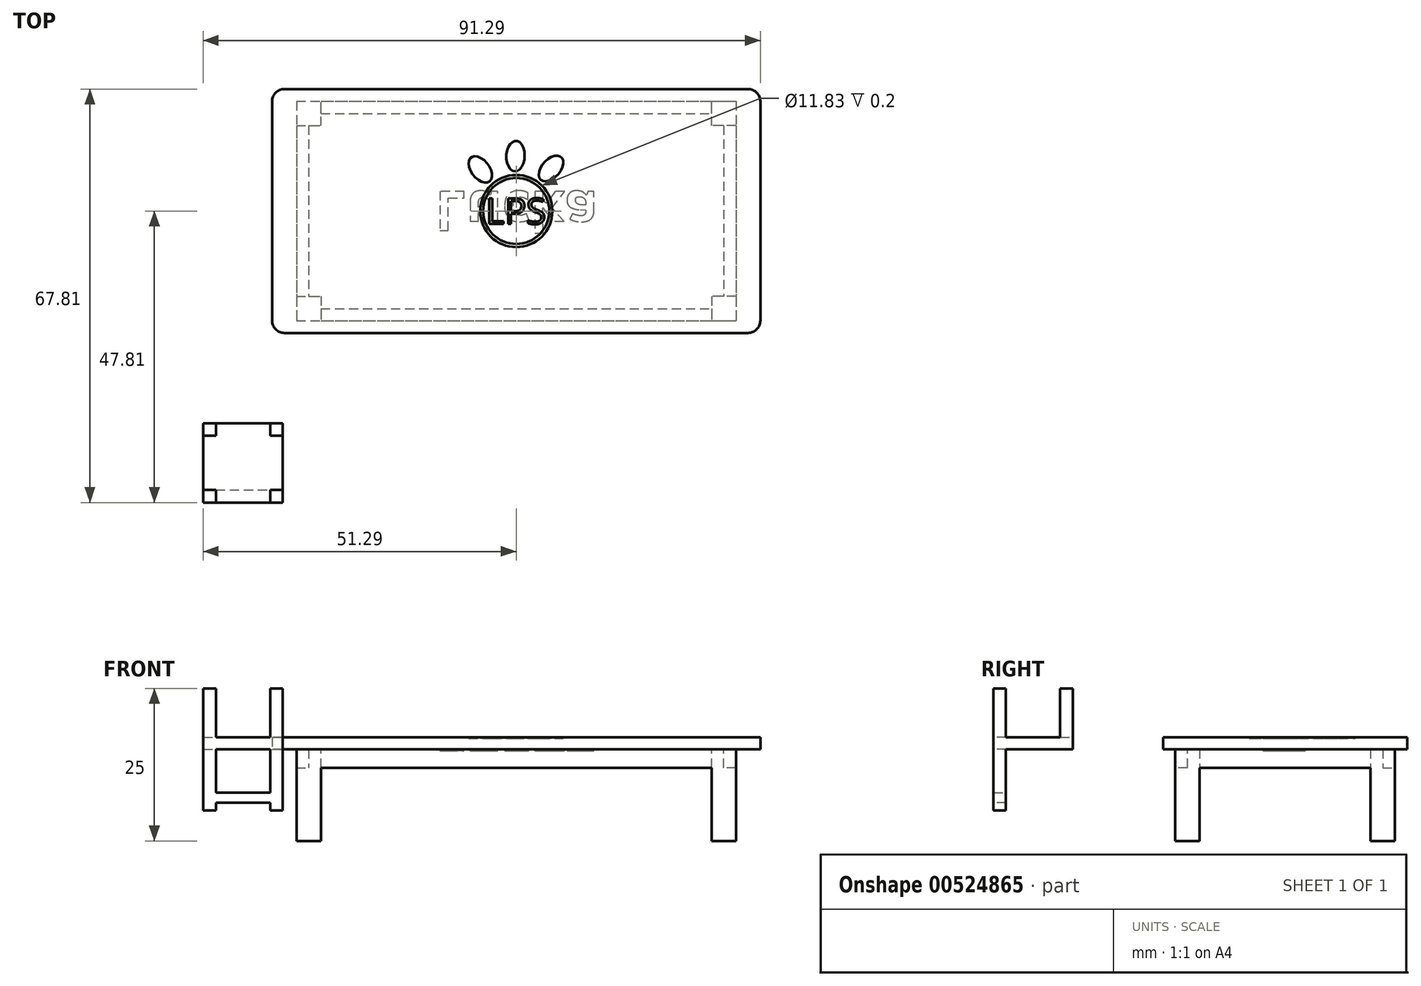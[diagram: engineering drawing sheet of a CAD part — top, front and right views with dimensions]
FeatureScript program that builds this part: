
annotation { "Feature Type Name" : "Feature", "Feature Type Description" : "" }
export const myFeature = defineFeature(function(context is Context, id is Id, definition is map)
    precondition{}
    {
        {
            assignVariable(context, id + "F0", {"name" : "vyska", "anyValue" : 40 * mm});
        }
        {
            var Q0;
            Q0=qCreatedBy(makeId("Top.planeOp"),FACE);
            var sketch = newSketch(context, id + "F1", { "sketchPlane" : qUnion([Q0])});
            skLineSegment(sketch, "E0.bottom", {"start": v(40, 20) * mm, "end": v(-40, 20) * mm});
            skLineSegment(sketch, "E0.top", {"start": v(40, -20) * mm, "end": v(-40, -20) * mm});
            skLineSegment(sketch, "E0.left", {"start": v(40, 20) * mm, "end": v(40, -20) * mm});
            skLineSegment(sketch, "E0.right", {"start": v(-40, 20) * mm, "end": v(-40, -20) * mm});
            skPoint(sketch, "E0.middle", {"position": v(0, 0) * mm});
            skSolve(sketch);
        }
        {
            assignVariable(context, id + "F2", {"name" : "tloustka_desky", "anyValue" : 2 * mm});
        }
        {
            var Q0;
            Q0=makeQuery(id+"F1.imprint","IMPRINT",FACE,{"disambiguationData":[TD([[makeQuery(id+"F1.imprint","IMPRINT",EDGE,{"derivedFrom":sQuery(id+"F1.wireOp",EDGE,"E0.bottom")}),1.0]])]});
            extrude(context, id + "F3", {"entities" : qUnion([Q0]), "depth" : getVariable(context, 'tloustka_desky'), "offsetDistance" : 25 * mm});
        }
        {
            var Q0;
            Q0=makeQuery(id+"F3.opExtrude","CAP_FACE",FACE,{"disambiguationData":[OSD([sQuery(id+"F1.wireOp",EDGE,"E0.bottom"),sQuery(id+"F1.wireOp",EDGE,"E0.top"),sQuery(id+"F1.wireOp",EDGE,"E0.left"),sQuery(id+"F1.wireOp",EDGE,"E0.right")])],"isStart":true});
            var sketch = newSketch(context, id + "F4", { "sketchPlane" : qUnion([Q0])});
            skLineSegment(sketch, "E1", {"start": v(-73.34, -36.67) * mm, "end": v(97.16, 48.58) * mm, "construction": true});
            skLineSegment(sketch, "E2", {"start": v(-70.65, 0) * mm, "end": v(92.9, 0) * mm, "construction": true});
            skLineSegment(sketch, "E3", {"start": v(0, 54.19) * mm, "end": v(0, -56.35) * mm, "construction": true});
            skLineSegment(sketch, "E4.bottom", {"start": v(-36, -18) * mm, "end": v(36, -18) * mm});
            skLineSegment(sketch, "E4.top", {"start": v(-36, 18) * mm, "end": v(36, 18) * mm});
            skLineSegment(sketch, "E4.left", {"start": v(-36, -18) * mm, "end": v(-36, 18) * mm});
            skLineSegment(sketch, "E4.right", {"start": v(36, -18) * mm, "end": v(36, 18) * mm});
            skPoint(sketch, "E4.middle", {"position": v(0, 0) * mm});
            skLineSegment(sketch, "E5", {"start": v(-36, -14) * mm, "end": v(-32, -14) * mm});
            skLineSegment(sketch, "E6", {"start": v(-32, -14) * mm, "end": v(-32, -18) * mm});
            skLineSegment(sketch, "E7.MirrorCS", {"start": v(36, -14) * mm, "end": v(32, -14) * mm});
            skLineSegment(sketch, "E8.MirrorCS", {"start": v(32, -14) * mm, "end": v(32, -18) * mm});
            skLineSegment(sketch, "E9.MirrorCS", {"start": v(-36, 14) * mm, "end": v(-32, 14) * mm});
            skLineSegment(sketch, "E10.MirrorCS", {"start": v(-32, 14) * mm, "end": v(-32, 18) * mm});
            skLineSegment(sketch, "E11.MirrorCS", {"start": v(32, 14) * mm, "end": v(32, 18) * mm});
            skLineSegment(sketch, "E12.MirrorCS", {"start": v(36, 14) * mm, "end": v(32, 14) * mm});
            skLineSegment(sketch, "E13.bottom", {"start": v(-34, -16) * mm, "end": v(34, -16) * mm});
            skLineSegment(sketch, "E13.top", {"start": v(-34, 16) * mm, "end": v(34, 16) * mm});
            skLineSegment(sketch, "E13.left", {"start": v(-34, -16) * mm, "end": v(-34, 16) * mm});
            skLineSegment(sketch, "E13.right", {"start": v(34, -16) * mm, "end": v(34, 16) * mm});
            skSolve(sketch);
        }
        {
            assignVariable(context, id + "F5", {"name" : "vyska", "anyValue" : 17 * mm});
        }
        {
            var Q0;
            {var subQ0=sQuery(id+"F4.wireOp",EDGE,"1s5hToEE-7Yhg-MsuK-7zEi-yVWtRCPxNcyl.left");var subQ1=sQuery(id+"F4.wireOp",EDGE,"1s5hToEE-7Yhg-MsuK-7zEi-yVWtRCPxNcyl.top");var subQ2=makeQuery(id+"F4.imprint","INTERSECT",VERTEX,{"derivedFrom":[subQ1,subQ0]});Q0=makeQuery(id+"F4.imprint","IMPRINT",FACE,{"disambiguationData":[TD([[makeQuery(id+"F4.imprint","IMPRINT",EDGE,{"disambiguationData":[TD([[subQ2,-1.0]])],"derivedFrom":subQ1}),-1.0]])]});}
            var Q1;
            {var subQ7=sQuery(id+"F4.wireOp",EDGE,"E4.left");var subQ8=sQuery(id+"F4.wireOp",EDGE,"E4.top");var subQ9=makeQuery(id+"F4.imprint","INTERSECT",VERTEX,{"derivedFrom":[subQ8,subQ7]});Q1=makeQuery(id+"F4.imprint","IMPRINT",FACE,{"disambiguationData":[TD([[makeQuery(id+"F4.imprint","IMPRINT",EDGE,{"disambiguationData":[TD([[subQ9,-1.0]])],"derivedFrom":subQ8}),-1.0]])]});}
            var Q2;
            {var subQ0=sQuery(id+"F4.wireOp",EDGE,"1s5hToEE-7Yhg-MsuK-7zEi-yVWtRCPxNcyl.right");var subQ1=sQuery(id+"F4.wireOp",EDGE,"1s5hToEE-7Yhg-MsuK-7zEi-yVWtRCPxNcyl.top");var subQ2=makeQuery(id+"F4.imprint","INTERSECT",VERTEX,{"derivedFrom":[subQ1,subQ0]});Q2=makeQuery(id+"F4.imprint","IMPRINT",FACE,{"disambiguationData":[TD([[makeQuery(id+"F4.imprint","IMPRINT",EDGE,{"disambiguationData":[TD([[subQ2,1.0]])],"derivedFrom":subQ1}),-1.0]])]});}
            var Q3;
            {var subQ7=sQuery(id+"F4.wireOp",EDGE,"E4.left");var subQ8=sQuery(id+"F4.wireOp",EDGE,"E4.bottom");var subQ9=makeQuery(id+"F4.imprint","INTERSECT",VERTEX,{"derivedFrom":[subQ8,subQ7]});Q3=makeQuery(id+"F4.imprint","IMPRINT",FACE,{"disambiguationData":[TD([[makeQuery(id+"F4.imprint","IMPRINT",EDGE,{"disambiguationData":[TD([[subQ9,-1.0]])],"derivedFrom":subQ8}),1.0]])]});}
            var Q4;
            {var subQ7=sQuery(id+"F4.wireOp",EDGE,"E4.right");var subQ8=sQuery(id+"F4.wireOp",EDGE,"E4.bottom");var subQ9=makeQuery(id+"F4.imprint","INTERSECT",VERTEX,{"derivedFrom":[subQ8,subQ7]});Q4=makeQuery(id+"F4.imprint","IMPRINT",FACE,{"disambiguationData":[TD([[makeQuery(id+"F4.imprint","IMPRINT",EDGE,{"disambiguationData":[TD([[subQ9,1.0]])],"derivedFrom":subQ8}),1.0]])]});}
            var Q5;
            {var subQ0=sQuery(id+"F4.wireOp",EDGE,"E10.MirrorCS");var subQ1=sQuery(id+"F4.wireOp",EDGE,"E9.MirrorCS");var subQ2=makeQuery(id+"F4.imprint","INTERSECT",VERTEX,{"derivedFrom":[subQ1,subQ0]});Q5=makeQuery(id+"F4.imprint","IMPRINT",FACE,{"disambiguationData":[TD([[makeQuery(id+"F4.imprint","IMPRINT",EDGE,{"disambiguationData":[TD([[subQ2,1.0]])],"derivedFrom":subQ1}),1.0]])]});}
            var Q6;
            {var subQ0=sQuery(id+"F4.wireOp",EDGE,"E6");var subQ1=sQuery(id+"F4.wireOp",EDGE,"E5");var subQ2=makeQuery(id+"F4.imprint","INTERSECT",VERTEX,{"derivedFrom":[subQ1,subQ0]});Q6=makeQuery(id+"F4.imprint","IMPRINT",FACE,{"disambiguationData":[TD([[makeQuery(id+"F4.imprint","IMPRINT",EDGE,{"disambiguationData":[TD([[subQ2,1.0]])],"derivedFrom":subQ1}),-1.0]])]});}
            var Q7;
            {var subQ0=sQuery(id+"F4.wireOp",EDGE,"E8.MirrorCS");var subQ1=sQuery(id+"F4.wireOp",EDGE,"E7.MirrorCS");var subQ2=makeQuery(id+"F4.imprint","INTERSECT",VERTEX,{"derivedFrom":[subQ1,subQ0]});Q7=makeQuery(id+"F4.imprint","IMPRINT",FACE,{"disambiguationData":[TD([[makeQuery(id+"F4.imprint","IMPRINT",EDGE,{"disambiguationData":[TD([[subQ2,1.0]])],"derivedFrom":subQ1}),1.0]])]});}
            var Q8;
            {var subQ0=sQuery(id+"F4.wireOp",EDGE,"E12.MirrorCS");var subQ1=sQuery(id+"F4.wireOp",EDGE,"E11.MirrorCS");var subQ2=makeQuery(id+"F4.imprint","INTERSECT",VERTEX,{"derivedFrom":[subQ1,subQ0]});Q8=makeQuery(id+"F4.imprint","IMPRINT",FACE,{"disambiguationData":[TD([[makeQuery(id+"F4.imprint","IMPRINT",EDGE,{"disambiguationData":[TD([[subQ2,-1.0]])],"derivedFrom":subQ1}),-1.0]])]});}
            var Q9;
            {var subQ1=sQuery(id+"F4.wireOp",EDGE,"E4.right");var subQ5=sQuery(id+"F4.wireOp",EDGE,"E4.top");var subQ6=makeQuery(id+"F4.imprint","INTERSECT",VERTEX,{"derivedFrom":[subQ5,subQ1]});Q9=makeQuery(id+"F4.imprint","IMPRINT",FACE,{"disambiguationData":[TD([[makeQuery(id+"F4.imprint","IMPRINT",EDGE,{"disambiguationData":[TD([[subQ6,1.0]])],"derivedFrom":subQ5}),-1.0]])]});}
            extrude(context, id + "F6", {"entities" : qUnion([Q0, Q1, Q2, Q3, Q4, Q5, Q6, Q7, Q8, Q9]), "operationType" : NewBodyOperationType.ADD, "depth" : getVariable(context, 'vyska') - getVariable(context, 'tloustka_desky'), "offsetDistance" : 25 * mm});
        }
        {
            var Q0;
            {var subQ0=sQuery(id+"F4.wireOp",EDGE,"E5");var subQ1=sQuery(id+"F4.wireOp",EDGE,"E4.left");var subQ2=makeQuery(id+"F4.imprint","INTERSECT",VERTEX,{"derivedFrom":[subQ1,subQ0]});Q0=makeQuery(id+"F4.imprint","IMPRINT",FACE,{"disambiguationData":[TD([[makeQuery(id+"F4.imprint","IMPRINT",EDGE,{"disambiguationData":[TD([[subQ2,-1.0]])],"derivedFrom":subQ1}),-1.0]])]});}
            var Q1;
            {var subQ0=sQuery(id+"F4.wireOp",EDGE,"E10.MirrorCS");var subQ1=sQuery(id+"F4.wireOp",EDGE,"E4.top");var subQ2=makeQuery(id+"F4.imprint","INTERSECT",VERTEX,{"derivedFrom":[subQ1,subQ0]});Q1=makeQuery(id+"F4.imprint","IMPRINT",FACE,{"disambiguationData":[TD([[makeQuery(id+"F4.imprint","IMPRINT",EDGE,{"disambiguationData":[TD([[subQ2,-1.0]])],"derivedFrom":subQ1}),-1.0]])]});}
            var Q2;
            {var subQ0=sQuery(id+"F4.wireOp",EDGE,"E7.MirrorCS");var subQ1=sQuery(id+"F4.wireOp",EDGE,"E4.right");var subQ2=makeQuery(id+"F4.imprint","INTERSECT",VERTEX,{"derivedFrom":[subQ1,subQ0]});Q2=makeQuery(id+"F4.imprint","IMPRINT",FACE,{"disambiguationData":[TD([[makeQuery(id+"F4.imprint","IMPRINT",EDGE,{"disambiguationData":[TD([[subQ2,-1.0]])],"derivedFrom":subQ1}),1.0]])]});}
            var Q3;
            {var subQ0=sQuery(id+"F4.wireOp",EDGE,"E6");var subQ1=sQuery(id+"F4.wireOp",EDGE,"E4.bottom");var subQ2=makeQuery(id+"F4.imprint","INTERSECT",VERTEX,{"derivedFrom":[subQ1,subQ0]});Q3=makeQuery(id+"F4.imprint","IMPRINT",FACE,{"disambiguationData":[TD([[makeQuery(id+"F4.imprint","IMPRINT",EDGE,{"disambiguationData":[TD([[subQ2,-1.0]])],"derivedFrom":subQ1}),1.0]])]});}
            var Q4;
            {var subQ1=sQuery(id+"F4.wireOp",EDGE,"E4.right");var subQ5=sQuery(id+"F4.wireOp",EDGE,"E4.top");var subQ6=makeQuery(id+"F4.imprint","INTERSECT",VERTEX,{"derivedFrom":[subQ5,subQ1]});Q4=makeQuery(id+"F4.imprint","IMPRINT",FACE,{"disambiguationData":[TD([[makeQuery(id+"F4.imprint","IMPRINT",EDGE,{"disambiguationData":[TD([[subQ6,1.0]])],"derivedFrom":subQ5}),-1.0]])]});}
            var Q5;
            {var subQ1=sQuery(id+"F4.wireOp",EDGE,"E4.left");var subQ9=sQuery(id+"F4.wireOp",EDGE,"E4.top");var subQ11=makeQuery(id+"F4.imprint","INTERSECT",VERTEX,{"derivedFrom":[subQ9,subQ1]});Q5=makeQuery(id+"F4.imprint","IMPRINT",FACE,{"disambiguationData":[TD([[makeQuery(id+"F4.imprint","IMPRINT",EDGE,{"disambiguationData":[TD([[subQ11,-1.0]])],"derivedFrom":subQ9}),-1.0]])]});}
            var Q6;
            {var subQ1=sQuery(id+"F4.wireOp",EDGE,"E4.left");var subQ7=sQuery(id+"F4.wireOp",EDGE,"E4.bottom");var subQ8=makeQuery(id+"F4.imprint","INTERSECT",VERTEX,{"derivedFrom":[subQ7,subQ1]});Q6=makeQuery(id+"F4.imprint","IMPRINT",FACE,{"disambiguationData":[TD([[makeQuery(id+"F4.imprint","IMPRINT",EDGE,{"disambiguationData":[TD([[subQ8,-1.0]])],"derivedFrom":subQ7}),1.0]])]});}
            var Q7;
            {var subQ1=sQuery(id+"F4.wireOp",EDGE,"E4.right");var subQ6=sQuery(id+"F4.wireOp",EDGE,"E4.bottom");var subQ11=makeQuery(id+"F4.imprint","INTERSECT",VERTEX,{"derivedFrom":[subQ6,subQ1]});Q7=makeQuery(id+"F4.imprint","IMPRINT",FACE,{"disambiguationData":[TD([[makeQuery(id+"F4.imprint","IMPRINT",EDGE,{"disambiguationData":[TD([[subQ11,1.0]])],"derivedFrom":subQ6}),1.0]])]});}
            extrude(context, id + "F7", {"entities" : qUnion([Q0, Q1, Q2, Q3, Q4, Q5, Q6, Q7]), "operationType" : NewBodyOperationType.ADD, "depth" : getVariable(context, 'tloustka_desky') * 1.5, "offsetDistance" : 25 * mm});
        }
        {
            var Q0;
            Q0=makeQuery(id+"F3.opExtrude","SWEPT_EDGE",EDGE,{"disambiguationData":[OSD([sQuery(id+"F1.wireOp",EDGE,"E0.top"),sQuery(id+"F1.wireOp",EDGE,"E0.right")])]});
            var Q1;
            Q1=makeQuery(id+"F3.opExtrude","SWEPT_EDGE",EDGE,{"disambiguationData":[OSD([sQuery(id+"F1.wireOp",EDGE,"E0.top"),sQuery(id+"F1.wireOp",EDGE,"E0.left")])]});
            var Q2;
            Q2=makeQuery(id+"F3.opExtrude","SWEPT_EDGE",EDGE,{"disambiguationData":[OSD([sQuery(id+"F1.wireOp",EDGE,"E0.bottom"),sQuery(id+"F1.wireOp",EDGE,"E0.left")])]});
            var Q3;
            Q3=makeQuery(id+"F3.opExtrude","SWEPT_EDGE",EDGE,{"disambiguationData":[OSD([sQuery(id+"F1.wireOp",EDGE,"E0.bottom"),sQuery(id+"F1.wireOp",EDGE,"E0.right")])]});
            fillet(context, id + "F8", {"entities" : qUnion([Q0, Q1, Q2, Q3]), "radius" : getVariable(context, 'tloustka_desky'), "tangentPropagation" : true, "allowEdgeOverflow" : false});
        }
        {
            var Q0;
            Q0=makeQuery(id+"F7.boolean.opBoolean","SPLIT",FACE,{"disambiguationData":[TD([makeQuery(id+"F6.opExtrude","SWEPT_FACE",FACE,{"disambiguationData":[OSD([sQuery(id+"F4.wireOp",EDGE,"E5")])]})])],"derivedFrom":makeQuery(id+"F3.opExtrude","CAP_FACE",FACE,{"disambiguationData":[OSD([sQuery(id+"F1.wireOp",EDGE,"E0.bottom"),sQuery(id+"F1.wireOp",EDGE,"E0.top"),sQuery(id+"F1.wireOp",EDGE,"E0.left"),sQuery(id+"F1.wireOp",EDGE,"E0.right")])],"isStart":true})});
            var sketch = newSketch(context, id + "F9", { "sketchPlane" : qUnion([Q0])});
            skText(sketch, "E14", { "text": "Lucka", "fontName": "OpenSans-Bold.ttf"});
            skLineSegment(sketch, "E15", {"start": v(-13.33, -3.25) * mm, "end": v(13.33, 3.25) * mm, "construction": true});
            skLineSegment(sketch, "E16", {"start": v(-13.33, 3.25) * mm, "end": v(13.33, -3.25) * mm, "construction": true});
            skPoint(sketch, "E17", {"position": v(0, 0) * mm});
            const initialGuessF9  = {"E14": [-0.01333, -0.00325, 1, 0, 0.0065]};
            skSetInitialGuess(sketch, initialGuessF9);
            skSolve(sketch);
        }
        {
            assignVariable(context, id + "F10", {"name" : "pismo", "anyValue" : 0.2 * mm});
        }
        {
            var Q0;
            Q0=makeQuery(id+"F9.imprint","IMPRINT",FACE,{"disambiguationData":[TD([[makeQuery(id+"F9.imprint","IMPRINT",EDGE,{"derivedFrom":sQuery(id+"F9.wireOp",EDGE,"E14.sketch_text.stroke-0")}),-1.0]])]});
            var Q1;
            Q1=makeQuery(id+"F9.imprint","IMPRINT",FACE,{"disambiguationData":[TD([[makeQuery(id+"F9.imprint","IMPRINT",EDGE,{"derivedFrom":sQuery(id+"F9.wireOp",EDGE,"E14.sketch_text.stroke-14")}),-1.0]])]});
            var Q2;
            Q2=makeQuery(id+"F9.imprint","IMPRINT",FACE,{"disambiguationData":[TD([[makeQuery(id+"F9.imprint","IMPRINT",EDGE,{"derivedFrom":sQuery(id+"F9.wireOp",EDGE,"E14.sketch_text.stroke-38")}),-1.0]])]});
            var Q3;
            Q3=makeQuery(id+"F9.imprint","IMPRINT",FACE,{"disambiguationData":[TD([[makeQuery(id+"F9.imprint","IMPRINT",EDGE,{"derivedFrom":sQuery(id+"F9.wireOp",EDGE,"E14.sketch_text.stroke-62")}),-1.0]])]});
            var Q4;
            Q4=makeQuery(id+"F9.imprint","IMPRINT",FACE,{"disambiguationData":[TD([[makeQuery(id+"F9.imprint","IMPRINT",EDGE,{"derivedFrom":sQuery(id+"F9.wireOp",EDGE,"E14.sketch_text.stroke-78")}),-1.0]])]});
            var Q5;
            Q5=makeQuery(id+"F9.imprint","IMPRINT",FACE,{"disambiguationData":[TD([[makeQuery(id+"F9.imprint","IMPRINT",EDGE,{"derivedFrom":sQuery(id+"F9.wireOp",EDGE,"E14.sketch_text.stroke-88")}),-1.0]])]});
            var Q6;
            Q6=makeQuery(id+"F9.imprint","IMPRINT",FACE,{"disambiguationData":[TD([[makeQuery(id+"F9.imprint","IMPRINT",EDGE,{"derivedFrom":sQuery(id+"F9.wireOp",EDGE,"E14.sketch_text.stroke-95")}),-1.0]])]});
            var Q7;
            Q7=makeQuery(id+"F9.imprint","IMPRINT",FACE,{"disambiguationData":[TD([[makeQuery(id+"F9.imprint","IMPRINT",EDGE,{"derivedFrom":sQuery(id+"F9.wireOp",EDGE,"E14.sketch_text.stroke-105")}),-1.0]])]});
            var Q8;
            Q8=makeQuery(id+"F9.imprint","IMPRINT",FACE,{"disambiguationData":[TD([[makeQuery(id+"F9.imprint","IMPRINT",EDGE,{"derivedFrom":sQuery(id+"F9.wireOp",EDGE,"E14.sketch_text.stroke-128")}),-1.0]])]});
            var Q9;
            Q9=makeQuery(id+"F9.imprint","IMPRINT",FACE,{"disambiguationData":[TD([[makeQuery(id+"F9.imprint","IMPRINT",EDGE,{"derivedFrom":sQuery(id+"F9.wireOp",EDGE,"E14.sketch_text.stroke-23")}),-1.0]])]});
            extrude(context, id + "F11", {"entities" : qUnion([Q0, Q1, Q2, Q3, Q4, Q5, Q6, Q7, Q8, Q9]), "operationType" : NewBodyOperationType.ADD, "depth" : getVariable(context, 'pismo'), "offsetDistance" : 25 * mm});
        }
        {
            var Q0;
            Q0=makeQuery(id+"F3.opExtrude","CAP_FACE",FACE,{"disambiguationData":[OSD([sQuery(id+"F1.wireOp",EDGE,"E0.bottom"),sQuery(id+"F1.wireOp",EDGE,"E0.top"),sQuery(id+"F1.wireOp",EDGE,"E0.left"),sQuery(id+"F1.wireOp",EDGE,"E0.right")])],"isStart":false});
            var sketch = newSketch(context, id + "F12", { "sketchPlane" : qUnion([Q0])});
            skText(sketch, "E18", { "text": "LPS", "fontName": "OpenSans-Regular.ttf"});
            skLineSegment(sketch, "E19", {"start": v(-4.98, -2.13) * mm, "end": v(4.98, 2.12) * mm, "construction": true});
            skLineSegment(sketch, "E20", {"start": v(-4.98, 2.13) * mm, "end": v(4.98, -2.13) * mm, "construction": true});
            skPoint(sketch, "E21", {"position": v(0, 0) * mm});
            skCircle(sketch, "E22", {"center": v(0, 0) * mm, "radius": 5.41 * mm});
            skCircle(sketch, "E23", {"center": v(0, 0) * mm, "radius": 5.91 * mm});
            skLineSegment(sketch, "E24", {"start": v(0, 0) * mm, "end": v(-7.22, 8.38) * mm, "construction": true});
            skEllipse(sketch, "E25", {"center": v(-5.88, 6.82) * mm, "majorRadius": 2.5 * mm, "minorRadius": 1.5 * mm, "majorAxis": v(0.61, -0.8)});
            skEllipse(sketch, "E26.1.0", {"center": v(-0.12, 9) * mm, "majorRadius": 2.5 * mm, "minorRadius": 1.5 * mm, "majorAxis": v(-0.04, -1)});
            skEllipse(sketch, "E26.2.0", {"center": v(5.7, 6.97) * mm, "majorRadius": 2.5 * mm, "minorRadius": 1.5 * mm, "majorAxis": v(-0.67, -0.74)});
            skLineSegment(sketch, "E26.anchor1", {"start": v(0, 0) * mm, "end": v(-5.88, 6.82) * mm, "construction": true});
            skLineSegment(sketch, "E26.anchor2", {"start": v(0, 0) * mm, "end": v(5.7, 6.97) * mm, "construction": true});
            const initialGuessF12  = {"E18": [-0.00498, -0.00213, 1, 0, 0.00425]};
            skSetInitialGuess(sketch, initialGuessF12);
            skSolve(sketch);
        }
        {
            var Q0;
            Q0=makeQuery(id+"F12.imprint","IMPRINT",FACE,{"disambiguationData":[TD([[makeQuery(id+"F12.imprint","IMPRINT",EDGE,{"derivedFrom":sQuery(id+"F12.wireOp",EDGE,"E18.sketch_text.stroke-0")}),-1.0]])]});
            var Q1;
            Q1=makeQuery(id+"F12.imprint","IMPRINT",FACE,{"disambiguationData":[TD([[makeQuery(id+"F12.imprint","IMPRINT",EDGE,{"derivedFrom":sQuery(id+"F12.wireOp",EDGE,"E18.sketch_text.stroke-6")}),-1.0]])]});
            var Q2;
            Q2=makeQuery(id+"F12.imprint","IMPRINT",FACE,{"disambiguationData":[TD([[makeQuery(id+"F12.imprint","IMPRINT",EDGE,{"derivedFrom":sQuery(id+"F12.wireOp",EDGE,"E18.sketch_text.stroke-21")}),-1.0]])]});
            var Q3;
            Q3=makeQuery(id+"F12.imprint","IMPRINT",FACE,{"disambiguationData":[TD([[makeQuery(id+"F12.imprint","IMPRINT",EDGE,{"derivedFrom":sQuery(id+"F12.wireOp",EDGE,"E22")}),-1.0]])]});
            var Q4;
            Q4=makeQuery(id+"F12.imprint","IMPRINT",FACE,{"disambiguationData":[TD([[makeQuery(id+"F12.imprint","IMPRINT",EDGE,{"derivedFrom":sQuery(id+"F12.wireOp",EDGE,"E25")}),1.0]])]});
            var Q5;
            Q5=makeQuery(id+"F12.imprint","IMPRINT",FACE,{"disambiguationData":[TD([[makeQuery(id+"F12.imprint","IMPRINT",EDGE,{"derivedFrom":sQuery(id+"F12.wireOp",EDGE,"E26.1.0")}),1.0]])]});
            var Q6;
            Q6=makeQuery(id+"F12.imprint","IMPRINT",FACE,{"disambiguationData":[TD([[makeQuery(id+"F12.imprint","IMPRINT",EDGE,{"derivedFrom":sQuery(id+"F12.wireOp",EDGE,"E26.2.0")}),1.0]])]});
            extrude(context, id + "F13", {"entities" : qUnion([Q0, Q1, Q2, Q3, Q4, Q5, Q6]), "operationType" : NewBodyOperationType.REMOVE, "oppositeDirection" : true, "depth" : getVariable(context, 'pismo'), "offsetDistance" : 25 * mm});
        }
        {
            var Q0;
            Q0=qCreatedBy(makeId("Top.planeOp"),FACE);
            var sketch = newSketch(context, id + "F14", { "sketchPlane" : qUnion([Q0])});
            skLineSegment(sketch, "E27.bottom", {"start": v(-51.29, -34.79) * mm, "end": v(-38.27, -34.79) * mm});
            skLineSegment(sketch, "E27.top", {"start": v(-51.29, -47.8) * mm, "end": v(-38.27, -47.8) * mm});
            skLineSegment(sketch, "E27.left", {"start": v(-51.29, -34.79) * mm, "end": v(-51.29, -47.8) * mm});
            skLineSegment(sketch, "E27.right", {"start": v(-38.27, -34.79) * mm, "end": v(-38.27, -47.8) * mm});
            skLineSegment(sketch, "E28", {"start": v(-51.29, -45.74) * mm, "end": v(-49.22, -45.74) * mm});
            skLineSegment(sketch, "E29", {"start": v(-49.22, -45.74) * mm, "end": v(-49.22, -47.8) * mm});
            skLineSegment(sketch, "E30", {"start": v(-54.35, -31.72) * mm, "end": v(-35.54, -50.53) * mm, "construction": true});
            skLineSegment(sketch, "E31", {"start": v(-54.73, -51.25) * mm, "end": v(-35.92, -32.44) * mm, "construction": true});
            skPoint(sketch, "E32", {"position": v(-44.78, -41.3) * mm});
            skLineSegment(sketch, "E33", {"start": v(-44.78, -30.52) * mm, "end": v(-44.78, -57.12) * mm, "construction": true});
            skLineSegment(sketch, "E34", {"start": v(-55.43, -41.3) * mm, "end": v(-28.83, -41.3) * mm, "construction": true});
            skLineSegment(sketch, "E35.MirrorCS", {"start": v(-40.34, -45.74) * mm, "end": v(-40.34, -47.8) * mm});
            skLineSegment(sketch, "E36.MirrorCS", {"start": v(-38.27, -45.74) * mm, "end": v(-40.34, -45.74) * mm});
            skLineSegment(sketch, "E37.MirrorCS", {"start": v(-51.29, -36.85) * mm, "end": v(-49.22, -36.85) * mm});
            skLineSegment(sketch, "E38.MirrorCS", {"start": v(-49.22, -36.85) * mm, "end": v(-49.22, -34.79) * mm});
            skLineSegment(sketch, "E39.MirrorCS", {"start": v(-40.34, -36.85) * mm, "end": v(-40.34, -34.79) * mm});
            skLineSegment(sketch, "E40.MirrorCS", {"start": v(-38.27, -36.85) * mm, "end": v(-40.34, -36.85) * mm});
            skSolve(sketch);
        }
        {
            var Q0;
            {var subQ4=sQuery(id+"F14.wireOp",EDGE,"E28");Q0=makeQuery(id+"F14.imprint","IMPRINT",FACE,{"disambiguationData":[TD([[makeQuery(id+"F14.imprint","IMPRINT",EDGE,{"derivedFrom":subQ4}),-1.0]])]});}
            var Q1;
            {var subQ3=sQuery(id+"F14.wireOp",EDGE,"E35.MirrorCS");Q1=makeQuery(id+"F14.imprint","IMPRINT",FACE,{"disambiguationData":[TD([[makeQuery(id+"F14.imprint","IMPRINT",EDGE,{"derivedFrom":subQ3}),1.0]])]});}
            extrude(context, id + "F15", {"entities" : qUnion([Q0, Q1]), "depth" : 10 * mm, "offsetDistance" : 25 * mm, "hasSecondDirection" : true, "secondDirectionOppositeDirection" : true, "secondDirectionDepth" : 10 * mm});
        }
        {
            var Q0;
            {var subQ4=sQuery(id+"F14.wireOp",EDGE,"E37.MirrorCS");Q0=makeQuery(id+"F14.imprint","IMPRINT",FACE,{"disambiguationData":[TD([[makeQuery(id+"F14.imprint","IMPRINT",EDGE,{"derivedFrom":subQ4}),1.0]])]});}
            var Q1;
            {var subQ3=sQuery(id+"F14.wireOp",EDGE,"E39.MirrorCS");Q1=makeQuery(id+"F14.imprint","IMPRINT",FACE,{"disambiguationData":[TD([[makeQuery(id+"F14.imprint","IMPRINT",EDGE,{"derivedFrom":subQ3}),-1.0]])]});}
            extrude(context, id + "F16", {"entities" : qUnion([Q0, Q1]), "depth" : 10 * mm, "offsetDistance" : 25 * mm});
        }
        {
            var Q0;
            {var subQ4=sQuery(id+"F14.wireOp",EDGE,"E28");Q0=makeQuery(id+"F14.imprint","IMPRINT",FACE,{"disambiguationData":[TD([[makeQuery(id+"F14.imprint","IMPRINT",EDGE,{"derivedFrom":subQ4}),1.0]])]});}
            var Q1;
            {var subQ4=sQuery(id+"F14.wireOp",EDGE,"E37.MirrorCS");Q1=makeQuery(id+"F14.imprint","IMPRINT",FACE,{"disambiguationData":[TD([[makeQuery(id+"F14.imprint","IMPRINT",EDGE,{"derivedFrom":subQ4}),1.0]])]});}
            var Q2;
            {var subQ3=sQuery(id+"F14.wireOp",EDGE,"E39.MirrorCS");Q2=makeQuery(id+"F14.imprint","IMPRINT",FACE,{"disambiguationData":[TD([[makeQuery(id+"F14.imprint","IMPRINT",EDGE,{"derivedFrom":subQ3}),-1.0]])]});}
            extrude(context, id + "F17", {"entities" : qUnion([Q0, Q1, Q2]), "operationType" : NewBodyOperationType.ADD, "depth" : 2 * mm, "offsetDistance" : 25 * mm});
        }
        {
            var Q0;
            {var subQ0=sQuery(id+"F14.wireOp",EDGE,"E36.MirrorCS");var subQ2=sQuery(id+"F14.wireOp",EDGE,"E27.top");var subQ4=sQuery(id+"F14.wireOp",EDGE,"E35.MirrorCS");var subQ5=sQuery(id+"F14.wireOp",EDGE,"E27.right");Q0=makeQuery(id+"F17.boolean.opBoolean","SPLIT",FACE,{"disambiguationData":[TD([makeQuery(id+"F15.opExtrude","CAP_FACE",FACE,{"disambiguationData":[OSD([subQ2,subQ5,subQ4,subQ0])],"isStart":true})])],"derivedFrom":makeQuery(id+"F15.opExtrude","SWEPT_FACE",FACE,{"disambiguationData":[OSD([subQ4])]})});}
            var sketch = newSketch(context, id + "F18", { "sketchPlane" : qUnion([Q0])});
            skLineSegment(sketch, "E41", {"start": v(47.8, -8.71) * mm, "end": v(45.74, -8.71) * mm});
            skLineSegment(sketch, "E42", {"start": v(47.8, -7.08) * mm, "end": v(45.74, -7.08) * mm});
            skSolve(sketch);
        }
        {
            var Q0;
            {var subQ0=sQuery(id+"F18.wireOp",EDGE,"E41");Q0=makeQuery(id+"F18.imprint","IMPRINT",FACE,{"disambiguationData":[TD([[makeQuery(id+"F18.imprint","IMPRINT",EDGE,{"derivedFrom":subQ0}),-1.0]])]});}
            extrude(context, id + "F19", {"entities" : qUnion([Q0]), "operationType" : NewBodyOperationType.ADD, "endBound" : BoundingType.UP_TO_NEXT, "depth" : 25 * mm, "offsetDistance" : 25 * mm});
        }
    });
